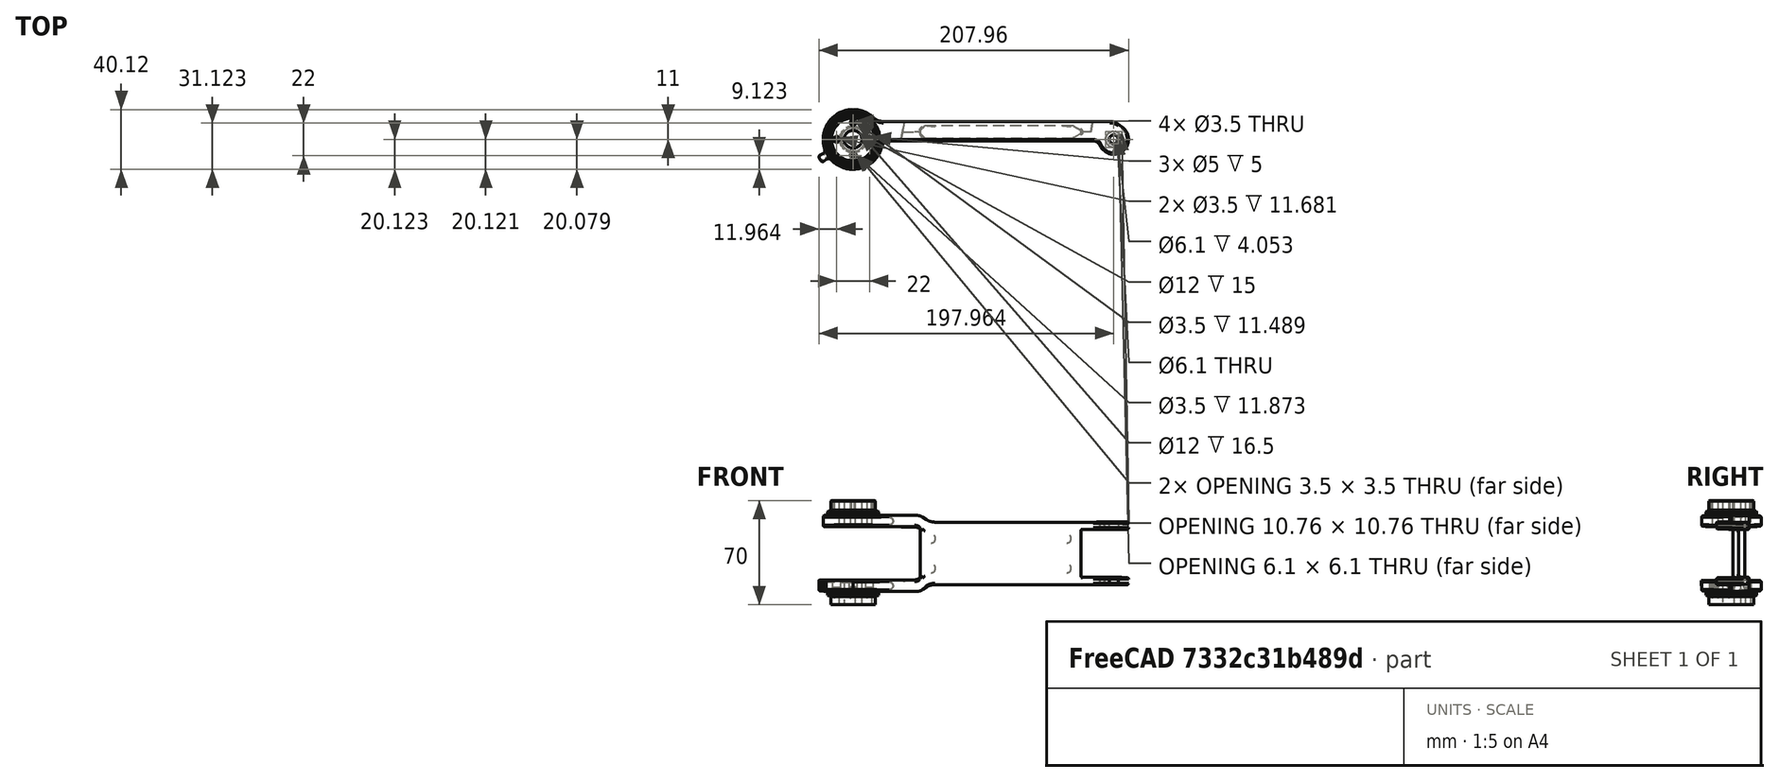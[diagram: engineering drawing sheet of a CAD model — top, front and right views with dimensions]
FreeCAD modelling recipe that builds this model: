
FCSTD DOCUMENT  (FreeCAD 0.21R33668 +26 (Git))
Label: 01
License: All rights reserved
LicenseURL: https://en.wikipedia.org/wiki/All_rights_reserved
objects: Part::Feature×1, PartDesign::FeatureBase×1, Sketcher::SketchObject×1, PartDesign::Body×1
note: 4 computed .brp shape members not serialized (recipe doc carries the construction recipe); baked Part::Feature solids carry a one-line shape summary decoded from their .brp

FEATURE [Part::Feature] Part__Feature  label="11_Robot_Link2_BaseControl_1_unit"
  shape: bbox 209.6 x 66.63 x 70.02 mm, 372 faces (baked)
FEATURE [PartDesign::FeatureBase] BaseFeature
  BaseFeature = -> Part__Feature
FEATURE [Sketcher::SketchObject] Sketch
  ExternalGeometry = -> [BaseFeature]
  FullyConstrained = true
  MapMode = 5
  Placement = pos=(0,-0.272634,15.6192) rot=(1,0,0;3.15905rad)
  Support = -> [BaseFeature]
  constraints (1):
    c: DistanceX(g-3,g-4) = 11
FEATURE [PartDesign::Body] Body
  BaseFeature = -> Part__Feature
  Group = -> [BaseFeature,Sketch]
  Origin = -> Origin
  Tip = -> BaseFeature
